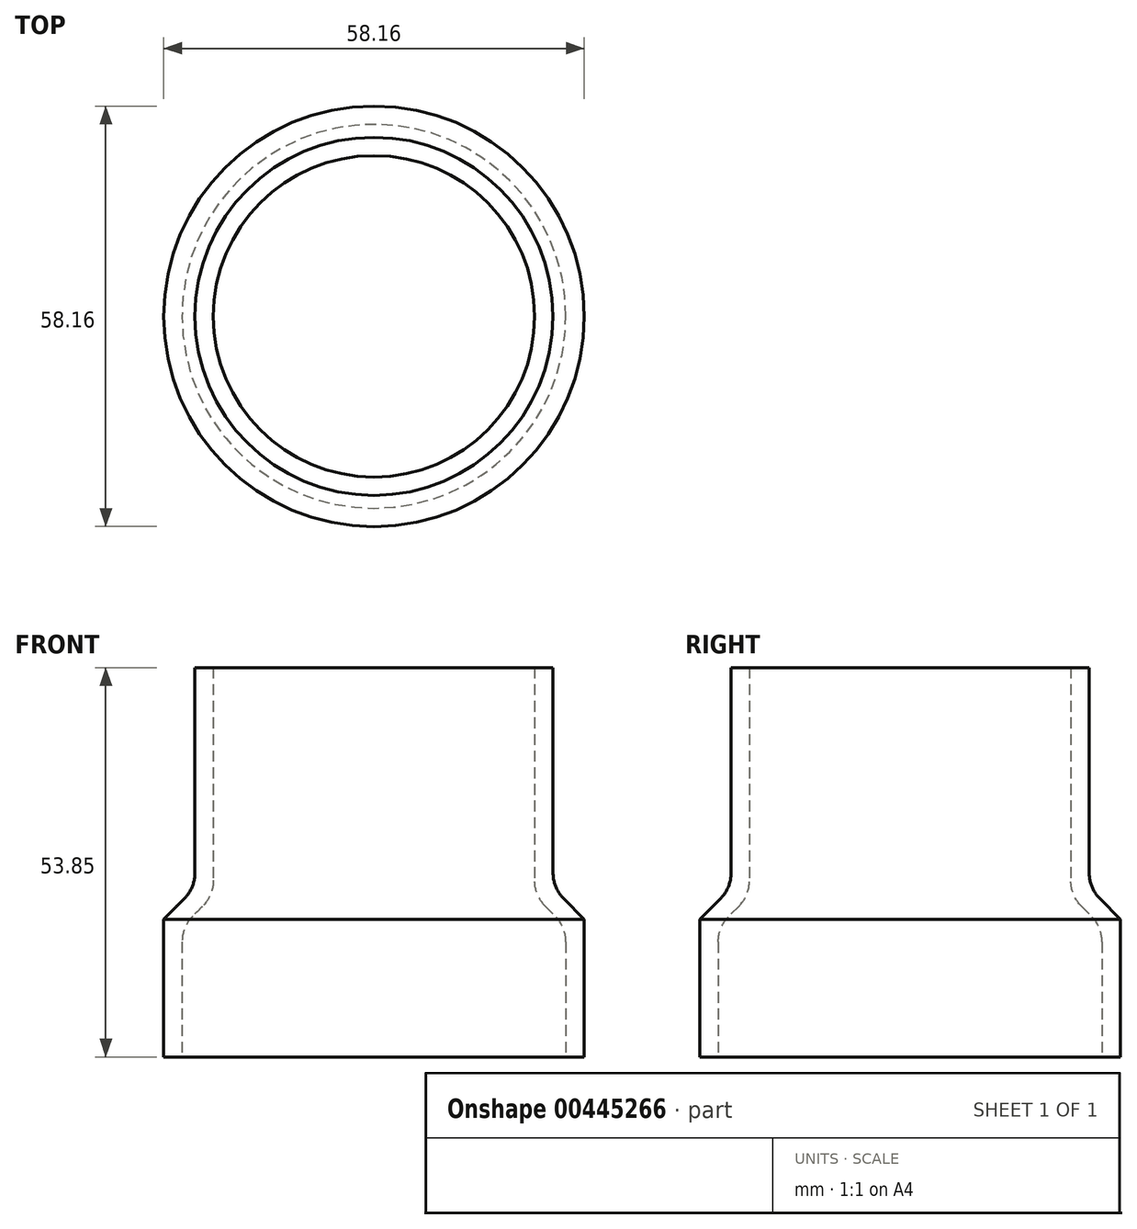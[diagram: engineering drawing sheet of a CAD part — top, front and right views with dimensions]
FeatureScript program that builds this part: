
annotation { "Feature Type Name" : "Feature", "Feature Type Description" : "" }
export const myFeature = defineFeature(function(context is Context, id is Id, definition is map)
    precondition{}
    {
        {
            var Q0;
            Q0=qCreatedBy(makeId("Right.planeOp"),FACE);
            var sketch = newSketch(context, id + "F0", { "sketchPlane" : qUnion([Q0])});
            skLineSegment(sketch, "E0", {"start": v(29.08, 0) * mm, "end": v(29.08, 19.05) * mm});
            skLineSegment(sketch, "E1", {"start": v(29.08, 0) * mm, "end": v(26.54, 0) * mm});
            skLineSegment(sketch, "E2", {"start": v(26.54, 0) * mm, "end": v(26.54, 18) * mm});
            skLineSegment(sketch, "E3", {"start": v(0, 0) * mm, "end": v(0, 54) * mm, "construction": true});
            skLineSegment(sketch, "E4", {"start": v(24.77, 23.37) * mm, "end": v(24.77, 53.85) * mm});
            skLineSegment(sketch, "E5", {"start": v(24.77, 53.85) * mm, "end": v(22.22, 53.85) * mm});
            skLineSegment(sketch, "E6", {"start": v(22.22, 53.85) * mm, "end": v(22.23, 22.32) * mm});
            skPoint(sketch, "E7.orphan", {"position": v(26.54, 15.29) * mm});
            skLineSegment(sketch, "E8", {"start": v(26.54, 18) * mm, "end": v(22.23, 22.32) * mm});
            skLineSegment(sketch, "E9", {"start": v(29.08, 19.05) * mm, "end": v(24.77, 23.37) * mm});
            skSolve(sketch);
        }
        {
            var Q0;
            Q0 = qSketchRegion(id + "F0", true);
            var Q1;
            Q1=sQuery(id+"F0.wireOp",EDGE,"E3");
            revolve(context, id + "F1", {"entities" : qUnion([Q0]), "axis" : qUnion([Q1]), "revolveType" : RevolveType.FULL});
        }
        {
            var Q0;
            Q0=makeQuery(id+"F1.opRevolve","SWEPT_EDGE",EDGE,{"disambiguationData":[OSD([sQuery(id+"F0.wireOp",EDGE,"E2"),sQuery(id+"F0.wireOp",EDGE,"E8")])]});
            var Q1;
            Q1=makeQuery(id+"F1.opRevolve","SWEPT_EDGE",EDGE,{"disambiguationData":[OSD([sQuery(id+"F0.wireOp",EDGE,"E6"),sQuery(id+"F0.wireOp",EDGE,"E8")])]});
            var Q2;
            Q2=makeQuery(id+"F1.opRevolve","SWEPT_EDGE",EDGE,{"disambiguationData":[OSD([sQuery(id+"F0.wireOp",EDGE,"E4"),sQuery(id+"F0.wireOp",EDGE,"E9")])]});
            fillet(context, id + "F2", {"entities" : qUnion([Q0, Q1, Q2]), "radius" : 5.08 * mm, "tangentPropagation" : true, "allowEdgeOverflow" : false});
        }
    });
